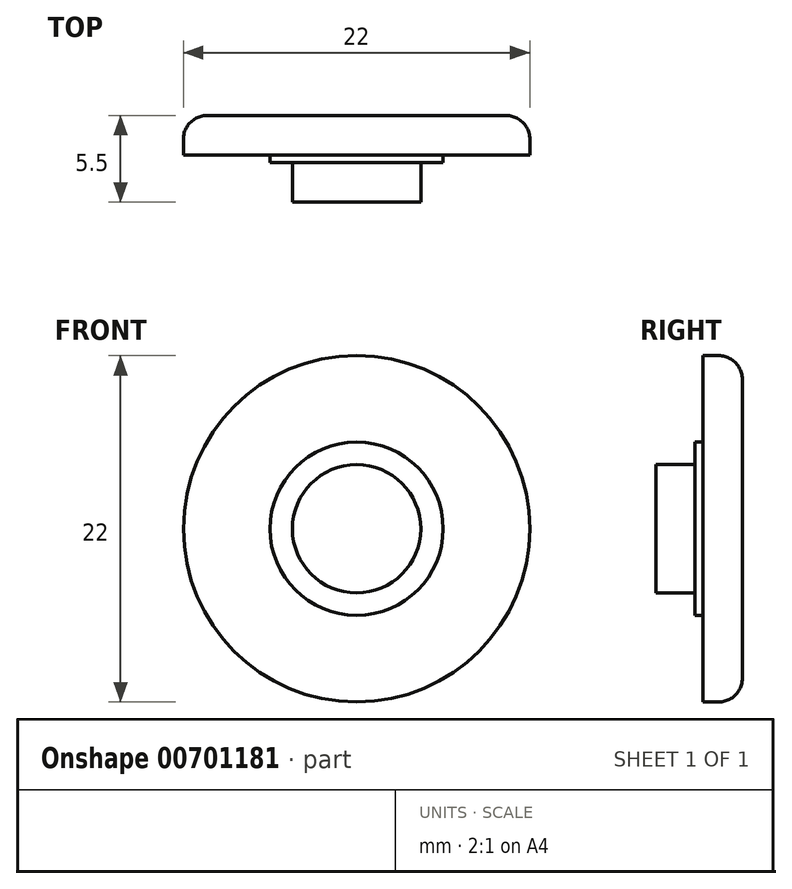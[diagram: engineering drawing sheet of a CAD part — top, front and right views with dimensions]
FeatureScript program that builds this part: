
annotation { "Feature Type Name" : "Feature", "Feature Type Description" : "" }
export const myFeature = defineFeature(function(context is Context, id is Id, definition is map)
    precondition{}
    {
        {
            var Q0;
            Q0=qCreatedBy(makeId("Front.planeOp"),FACE);
            var sketch = newSketch(context, id + "F0", { "sketchPlane" : qUnion([Q0])});
            skCircle(sketch, "E0", {"center": v(0, 0) * mm, "radius": 11 * mm});
            skCircle(sketch, "E1", {"center": v(0, 0) * mm, "radius": 5.5 * mm});
            skCircle(sketch, "E2", {"center": v(0, 0) * mm, "radius": 4.08 * mm});
            skSolve(sketch);
        }
        {
            var Q0;
            Q0=makeQuery(id+"F0.imprint","IMPRINT",FACE,{"disambiguationData":[TD([[makeQuery(id+"F0.imprint","IMPRINT",EDGE,{"derivedFrom":sQuery(id+"F0.wireOp",EDGE,"E0")}),1.0]])]});
            extrude(context, id + "F1", {"entities" : qUnion([Q0]), "depth" : 2.5 * mm, "offsetDistance" : 25 * mm});
        }
        {
            var Q0;
            Q0=makeQuery(id+"F0.imprint","IMPRINT",FACE,{"disambiguationData":[TD([[makeQuery(id+"F0.imprint","IMPRINT",EDGE,{"derivedFrom":sQuery(id+"F0.wireOp",EDGE,"E1")}),1.0]])]});
            extrude(context, id + "F2", {"entities" : qUnion([Q0]), "operationType" : NewBodyOperationType.ADD, "depth" : 3 * mm, "offsetDistance" : 25 * mm});
        }
        {
            var Q0;
            Q0=makeQuery(id+"F0.imprint","IMPRINT",FACE,{"disambiguationData":[TD([[makeQuery(id+"F0.imprint","IMPRINT",EDGE,{"derivedFrom":sQuery(id+"F0.wireOp",EDGE,"E2")}),1.0]])]});
            extrude(context, id + "F3", {"entities" : qUnion([Q0]), "operationType" : NewBodyOperationType.ADD, "depth" : 5.5 * mm, "offsetDistance" : 25 * mm});
        }
        {
            var Q0;
            Q0=makeQuery(id+"F1.opExtrude","CAP_EDGE",EDGE,{"disambiguationData":[OSD([sQuery(id+"F0.wireOp",EDGE,"E0")])],"isStart":true});
            fillet(context, id + "F4", {"entities" : qUnion([Q0]), "radius" : 1.5 * mm, "tangentPropagation" : true, "allowEdgeOverflow" : false});
        }
    });
